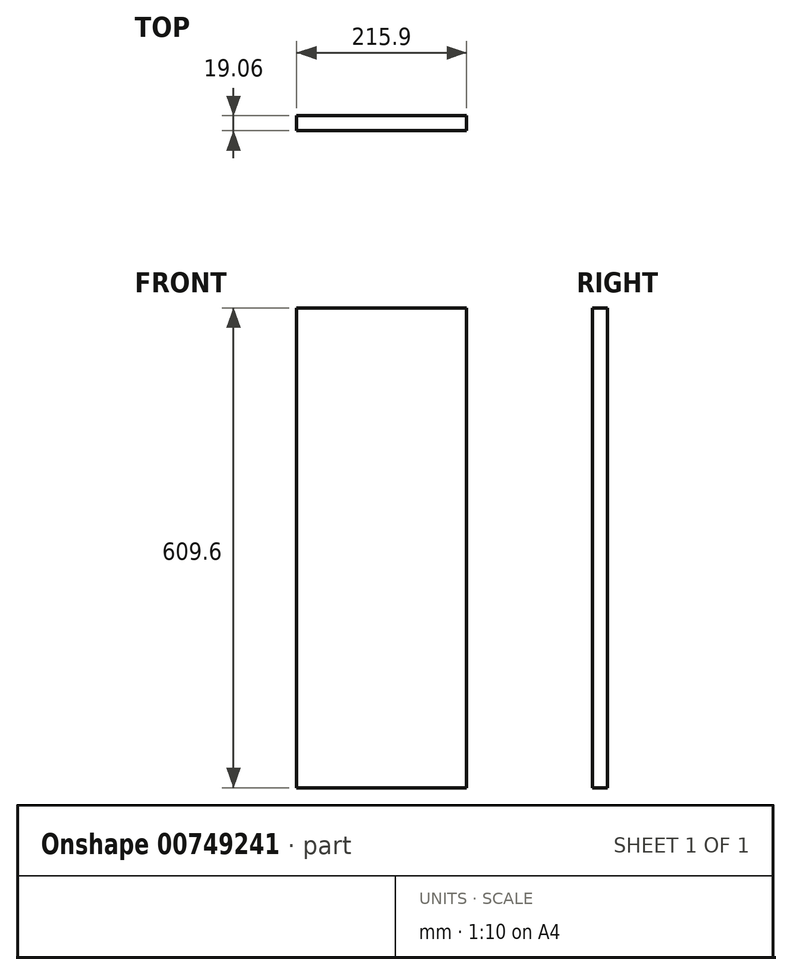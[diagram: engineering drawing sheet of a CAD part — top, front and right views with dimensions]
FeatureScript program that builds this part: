
annotation { "Feature Type Name" : "Feature", "Feature Type Description" : "" }
export const myFeature = defineFeature(function(context is Context, id is Id, definition is map)
    precondition{}
    {
        {
            var Q0;
            Q0=qCreatedBy(makeId("Top.planeOp"),FACE);
            var sketch = newSketch(context, id + "F0", { "sketchPlane" : qUnion([Q0])});
            skLineSegment(sketch, "E0.bottom", {"start": v(107.95, 9.53) * mm, "end": v(-107.95, 9.53) * mm});
            skLineSegment(sketch, "E0.top", {"start": v(107.95, -9.53) * mm, "end": v(-107.95, -9.53) * mm});
            skLineSegment(sketch, "E0.left", {"start": v(107.95, 9.53) * mm, "end": v(107.95, -9.53) * mm});
            skLineSegment(sketch, "E0.right", {"start": v(-107.95, 9.53) * mm, "end": v(-107.95, -9.53) * mm});
            skPoint(sketch, "E0.middle", {"position": v(0, 0) * mm});
            skSolve(sketch);
        }
        {
            var Q0;
            Q0 = qSketchRegion(id + "F0", true);
            extrude(context, id + "F1", {"entities" : qUnion([Q0]), "depth" : 609.6 * mm, "offsetDistance" : 25.4 * mm});
        }
    });
